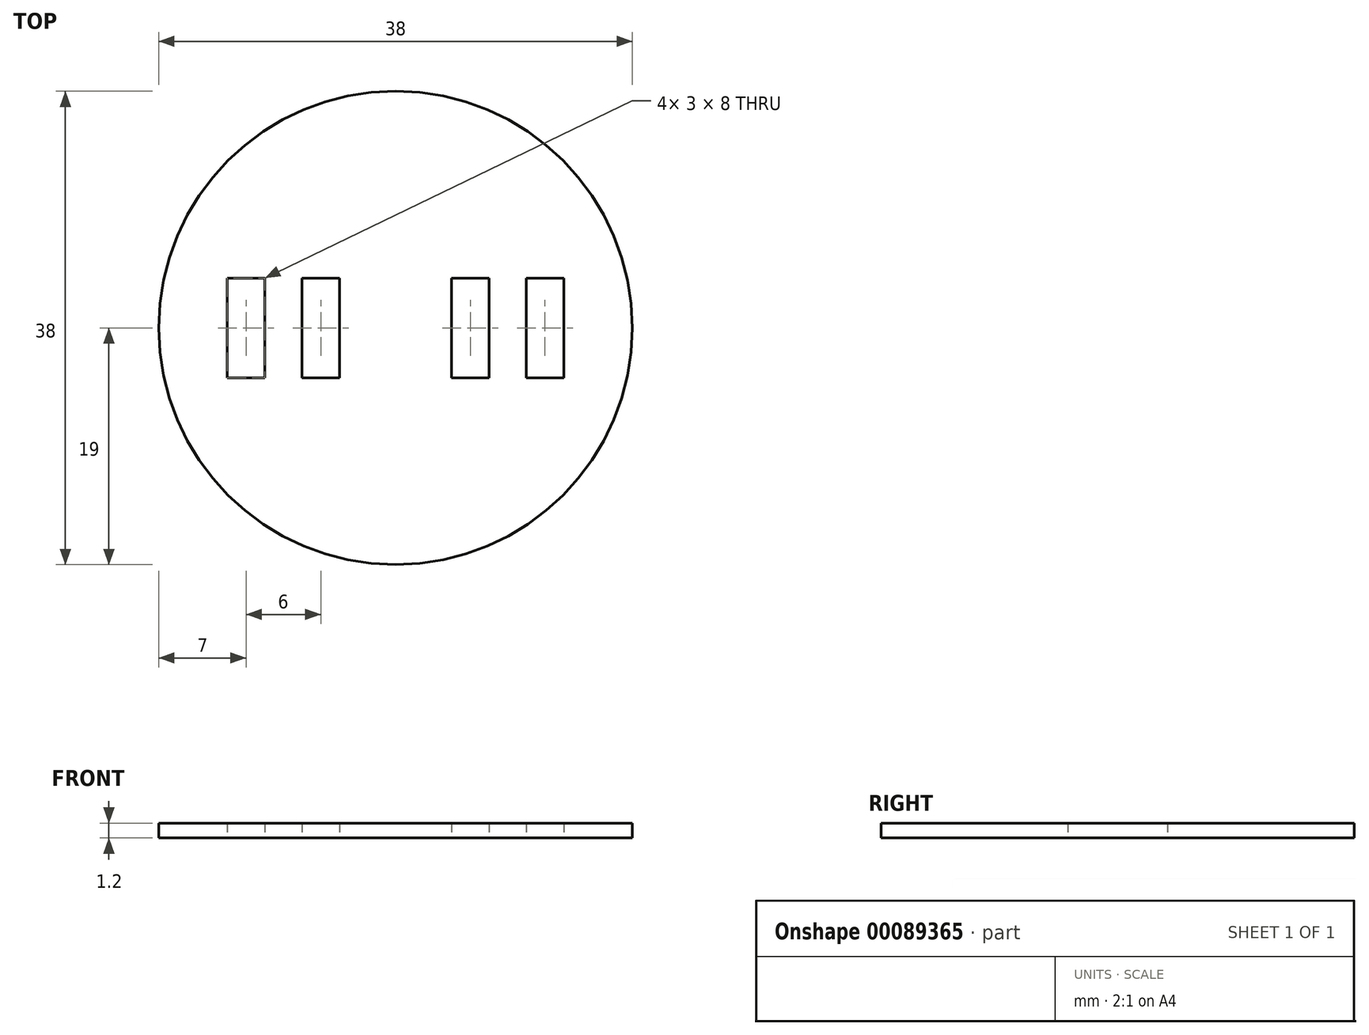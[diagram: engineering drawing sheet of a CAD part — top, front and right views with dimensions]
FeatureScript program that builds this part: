
annotation { "Feature Type Name" : "Feature", "Feature Type Description" : "" }
export const myFeature = defineFeature(function(context is Context, id is Id, definition is map)
    precondition{}
    {
        {
            var Q0;
            Q0=qCreatedBy(makeId("Top.planeOp"),FACE);
            var sketch = newSketch(context, id + "F0", { "sketchPlane" : qUnion([Q0])});
            skCircle(sketch, "E0", {"center": v(0, 0) * mm, "radius": 19 * mm});
            skLineSegment(sketch, "E1.bottom", {"start": v(-13.5, 4) * mm, "end": v(-10.5, 4) * mm});
            skLineSegment(sketch, "E1.top", {"start": v(-13.5, -4) * mm, "end": v(-10.5, -4) * mm});
            skLineSegment(sketch, "E1.left", {"start": v(-13.5, 4) * mm, "end": v(-13.5, -4) * mm});
            skLineSegment(sketch, "E1.right", {"start": v(-10.5, 4) * mm, "end": v(-10.5, -4) * mm});
            skLineSegment(sketch, "E2.1.0.0", {"start": v(-4.5, 4) * mm, "end": v(-4.5, -4) * mm});
            skLineSegment(sketch, "E2.1.0.1", {"start": v(-7.5, 4) * mm, "end": v(-7.5, -4) * mm});
            skLineSegment(sketch, "E2.1.0.2", {"start": v(-7.5, -4) * mm, "end": v(-4.5, -4) * mm});
            skLineSegment(sketch, "E2.1.0.3", {"start": v(-7.5, 4) * mm, "end": v(-4.5, 4) * mm});
            skLineSegment(sketch, "E2.direction1", {"start": v(-10.5, -4) * mm, "end": v(-4.5, -4) * mm, "construction": true});
            skLineSegment(sketch, "E3.1.0.0", {"start": v(7.5, 4) * mm, "end": v(7.5, -4) * mm});
            skLineSegment(sketch, "E3.1.0.1", {"start": v(4.5, 4) * mm, "end": v(4.5, -4) * mm});
            skLineSegment(sketch, "E3.1.0.2", {"start": v(10.5, 4) * mm, "end": v(10.5, -4) * mm});
            skLineSegment(sketch, "E3.1.0.3", {"start": v(13.5, 4) * mm, "end": v(13.5, -4) * mm});
            skLineSegment(sketch, "E3.1.0.4", {"start": v(4.5, 4) * mm, "end": v(7.5, 4) * mm});
            skLineSegment(sketch, "E3.1.0.5", {"start": v(4.5, -4) * mm, "end": v(7.5, -4) * mm});
            skLineSegment(sketch, "E3.1.0.6", {"start": v(10.5, 4) * mm, "end": v(13.5, 4) * mm});
            skLineSegment(sketch, "E3.1.0.7", {"start": v(10.5, -4) * mm, "end": v(13.5, -4) * mm});
            skLineSegment(sketch, "E3.1.0.8", {"start": v(7.5, -4) * mm, "end": v(13.5, -4) * mm, "construction": true});
            skLineSegment(sketch, "E3.direction1", {"start": v(-10.5, -4) * mm, "end": v(7.5, -4) * mm, "construction": true});
            skLineSegment(sketch, "E3.direction2", {"start": v(-10.5, -4) * mm, "end": v(-10.5, -4) * mm});
            skPoint(sketch, "E4", {"position": v(-13.5, 0) * mm});
            skLineSegment(sketch, "E5", {"start": v(-13.5, 0) * mm, "end": v(13.5, 0) * mm, "construction": true});
            skSolve(sketch);
        }
        {
            var Q0;
            Q0 = qSketchRegion(id + "F0", true);
            extrude(context, id + "F1", {"entities" : qUnion([Q0]), "depth" : 1.2 * mm});
        }
    });
